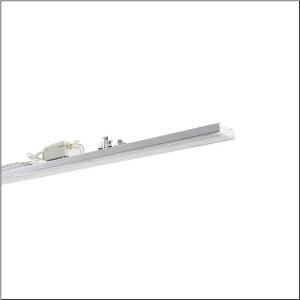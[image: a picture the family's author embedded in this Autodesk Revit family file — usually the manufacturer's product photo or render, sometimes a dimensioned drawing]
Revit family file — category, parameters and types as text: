
# Revit family: licross_r__21_recessed_mo_52tl12dv4dxg_386a
name_source: partatom
category: Lighting Fixtures
units: mm (PartAtom-declared; Revit-internal decimal feet)

## family parameters
Cut with Voids When Loaded = No
Host = Face
Light Source = No
Part Type = Normal
Room Calculation Point = No
Round Connector Dimension = Use Diameter
Shared = No

## types (1)
- --- (1 x LED, 13000 lm, 71 W, 4000K)
    Apparent Load = 71 VA
    CIE Flux Codes = 72 92 99 100 100
    Color Rendering = 80
    Color Temperature = 4000K
    Default Elevation = 1800 mm
    Description = Licross® 21 Recessed MO, luminaire insert, of sheet steel, galvanised, coil coated, white, length: 2.250mm, width: 66mm, height: 67mm, LED rated luminous flux: 13.000lm, light colour: 840, control gear: DALI 2, with plug, 5-pole, with phase selection, mains connection: 220..240V, AC, 50/60Hz, rated input power: 71W, halogen-free wiring, primary optical cover: cover, of PMMA, light emission: direct distribution, primary light characteristic: symmetric, protection rating (complete): IP40, insulation class (complete): insulation class I (protective earthing), certification: CE, ENEC, VDE, UKCA, protection symbol: D if used in an environment without relevant dust loads with corresponding accessories, impact resistance: IK06, permissible ambient temperature for indoor applications: -25..+35°C, corresponds to IFS (International Featured Standards) requirements for safety and quality in the food industry, reducing of maximum allowable ambient temperature of 5°C with ceiling mounting, LABS conformity tested according to VDMA 24364:2018-05, packaging unit: 1 piece
    Height = 58 mm
    Lamp = 1 x LED
    Lamp Light Flux = 13000 lm
    Lamp Power = 71 W
    Lamp count = 1
    Length = 2250 mm
    Luminous efficacy = 183 lm/W
    Manufacturer = Siteco
    ModVariant = No
    Model = 52TL12DV4DXG
    Mounting Place = Ceiling
    Mounting Type = Pendant
    Number of Poles = 1
    OnlyDefault = Yes
    Power Factor = 1
    Product Name = Licross® 21 Recessed MO
    Product group = luminaire insert
    ProductGroupID = 901
    Protection Class = Protection class I
    Protection Degree = IP 40
    RLX_Detail_Level = 1
    RLX_Emergency_Light_Flux = 0 lm
    RLX_Emergency_Type = 0
    RLX_Emergency_Type_DB = No
    RlxData = <blob elided: 29457 chars, md5=6891cf58>
    Socket = socket
    Standby Power = 0 W
    System Light Flux = 13000 lm
    System Power = 71 W
    Type Comments = factory setting: luminous flux: 100 % | dim-lin: 254 | 324 mA
    Type Image = l_1296930.jpg
    URL = http://relux.com
    VarID = @adj_057989
    Voltage = 0 V
    Weight = 0.00 kg
    Width = 66 mm

## geometry (parser evidence)
native form markers: Blend x4, Sweep x9
no freeform markers — native parametric forms only
